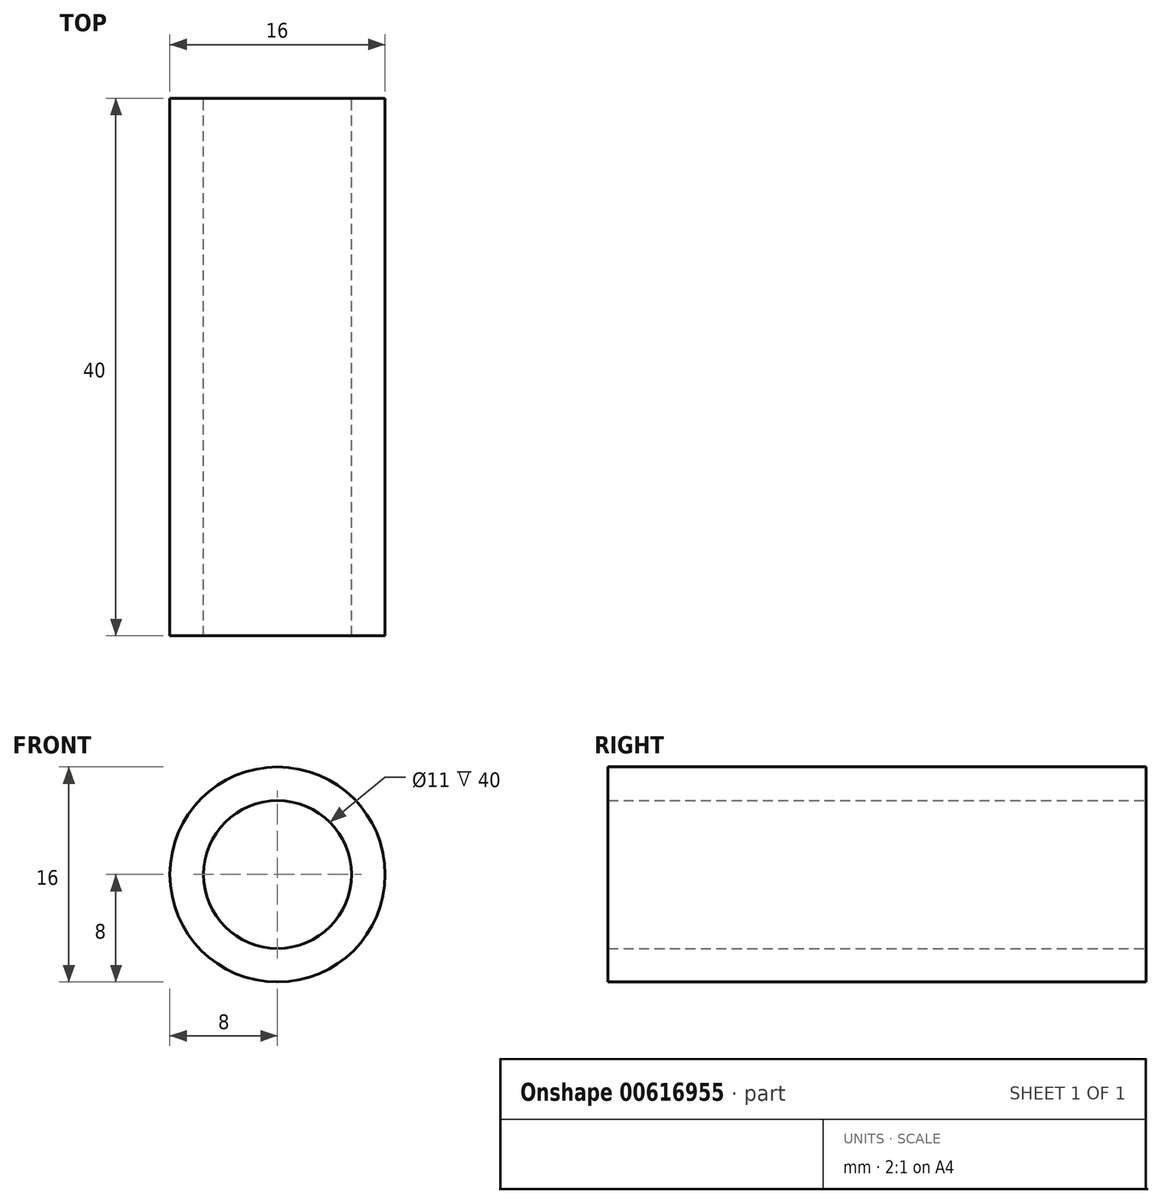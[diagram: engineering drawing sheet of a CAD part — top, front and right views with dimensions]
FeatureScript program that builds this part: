
annotation { "Feature Type Name" : "Feature", "Feature Type Description" : "" }
export const myFeature = defineFeature(function(context is Context, id is Id, definition is map)
    precondition{}
    {
        {
            var Q0;
            Q0=qCreatedBy(makeId("Front.planeOp"),FACE);
            var sketch = newSketch(context, id + "F0", { "sketchPlane" : qUnion([Q0])});
            skCircle(sketch, "E0", {"center": v(0, 0) * mm, "radius": 5.5 * mm});
            skCircle(sketch, "E1", {"center": v(0, 0) * mm, "radius": 8 * mm});
            skSolve(sketch);
        }
        {
            var Q0;
            Q0 = qSketchRegion(id + "F0", true);
            extrude(context, id + "F1", {"entities" : qUnion([Q0]), "depth" : 40 * mm, "offsetDistance" : 25 * mm});
        }
    });
